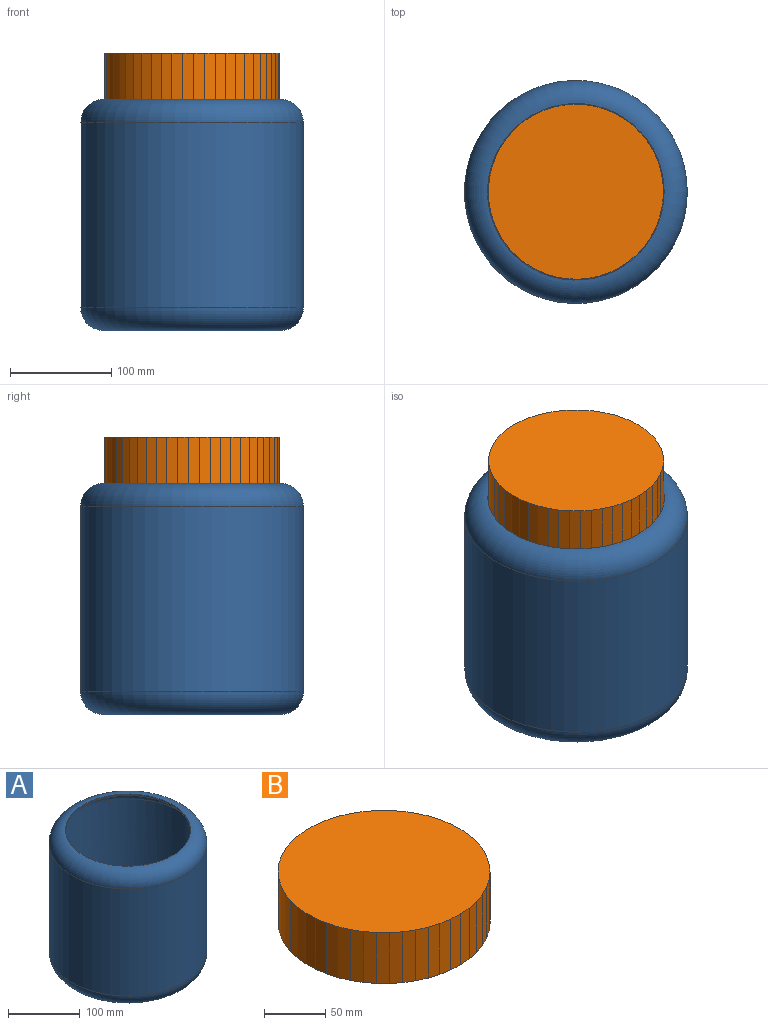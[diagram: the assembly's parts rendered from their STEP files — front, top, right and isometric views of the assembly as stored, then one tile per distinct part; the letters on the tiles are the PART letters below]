
ASSEMBLY  parts=2 mates=1
PART A: 9 faces, bbox 238.4x238.4x228.6 mm
  f0: cylinder r=110.11mm len=220.23mm, axis (0,0,-1), area 126529.7mm2, adj f2,f3
  f1: plane 174.51x174.51mm, normal (0,0,-1), area 23918.3mm2, adj f3
  f2: torus R=87.25mm, axis (0,0,1), area 22969.9mm2, adj f0,f4
  f3: torus R=87.25mm, axis (0,0,1), area 22969.9mm2, adj f0,f1
  f4: cylinder r=87.25mm len=174.51mm, axis (0,0,1), area 1392.5mm2, adj f2,f7
  f5: cylinder r=107.57mm len=215.15mm, axis (0,0,-1), area 123611.1mm2, adj f7,f8
  f6: plane 174.51x174.51mm, normal (0,0,1), area 23918.3mm2, adj f8
  f7: torus R=87.25mm, axis (0,0,1), area 20093.4mm2, adj f4,f5
  f8: torus R=87.25mm, axis (0,0,1), area 20093.4mm2, adj f5,f6
PART B: 52 faces, bbox 172.9x173x50.8 mm
  f0: plane 50.8x9.63mm, normal (0.89,-0.46,0), area 551.9mm2, adj f1,f49,f50,f51
  f1: plane 50.8x10.18mm, normal (0.94,-0.35,0), area 551.9mm2, adj f0,f2,f50,f51
  f2: plane 50.8x10.58mm, normal (0.97,-0.23,0), area 551.9mm2, adj f1,f3,f50,f51
  f3: plane 50.8x10.81mm, normal (0.99,-0.1,0), area 551.9mm2, adj f2,f4,f50,f51
  f4: plane 50.8x10.86mm, normal (1,0.02,0), area 551.9mm2, adj f3,f5,f50,f51
  f5: plane 50.8x10.75mm, normal (0.99,0.15,0), area 551.9mm2, adj f4,f6,f50,f51
  f6: plane 50.8x10.46mm, normal (0.96,0.27,0), area 551.9mm2, adj f5,f7,f50,f51
  f7: plane 50.8x10.02mm, normal (0.92,0.39,0), area 551.9mm2, adj f6,f8,f50,f51
  f8: plane 50.8x9.41mm, normal (0.87,0.5,0), area 551.9mm2, adj f7,f9,f50,f51
  f9: plane 50.8x8.65mm, normal (0.8,0.6,0), area 551.9mm2, adj f8,f10,f50,f51
  f10: plane 50.8x7.76mm, normal (0.71,0.7,0), area 551.9mm2, adj f9,f11,f50,f51
  f11: plane 50.8x8.52mm, normal (0.62,0.78,0), area 551.9mm2, adj f10,f12,f50,f51
  f12: plane 50.8x9.3mm, normal (0.52,0.86,0), area 551.9mm2, adj f11,f13,f50,f51
  f13: plane 50.8x9.93mm, normal (0.41,0.91,0), area 551.9mm2, adj f12,f14,f50,f51
  f14: plane 50.8x10.4mm, normal (0.29,0.96,0), area 551.9mm2, adj f13,f15,f50,f51
  f15: plane 50.8x10.71mm, normal (0.17,0.99,0), area 551.9mm2, adj f14,f16,f50,f51
  f16: plane 50.8x10.86mm, normal (0.04,1,0), area 551.9mm2, adj f15,f17,f50,f51
  f17: plane 50.8x10.83mm, normal (-0.08,1,0), area 551.9mm2, adj f16,f18,f50,f51
  f18: plane 50.8x10.63mm, normal (-0.21,0.98,0), area 551.9mm2, adj f17,f19,f50,f51
  f19: plane 50.8x10.26mm, normal (-0.33,0.94,0), area 551.9mm2, adj f18,f20,f50,f51
  f20: plane 50.8x9.73mm, normal (-0.44,0.9,0), area 551.9mm2, adj f19,f21,f50,f51
  f21: plane 50.8x9.05mm, normal (-0.55,0.83,0), area 551.9mm2, adj f20,f22,f50,f51
  f22: plane 50.8x8.22mm, normal (-0.65,0.76,0), area 551.9mm2, adj f21,f23,f50,f51
  f23: plane 50.8x8.08mm, normal (-0.74,0.67,0), area 551.9mm2, adj f22,f24,f50,f51
  f24: plane 50.8x8.92mm, normal (-0.82,0.57,0), area 551.9mm2, adj f23,f25,f50,f51
  f25: plane 50.8x9.63mm, normal (-0.89,0.46,0), area 551.9mm2, adj f24,f26,f50,f51
  f26: plane 50.8x10.18mm, normal (-0.94,0.35,0), area 551.9mm2, adj f25,f27,f50,f51
  f27: plane 50.8x10.58mm, normal (-0.97,0.23,0), area 551.9mm2, adj f26,f28,f50,f51
  f28: plane 50.8x10.81mm, normal (-0.99,0.1,0), area 551.9mm2, adj f27,f29,f50,f51
  f29: plane 50.8x10.86mm, normal (-1,-0.02,0), area 551.9mm2, adj f28,f30,f50,f51
  f30: plane 50.8x10.75mm, normal (-0.99,-0.15,0), area 551.9mm2, adj f29,f31,f50,f51
  f31: plane 50.8x10.46mm, normal (-0.96,-0.27,0), area 551.9mm2, adj f30,f32,f50,f51
  f32: plane 50.8x10.02mm, normal (-0.92,-0.39,0), area 551.9mm2, adj f31,f33,f50,f51
  f33: plane 50.8x9.41mm, normal (-0.87,-0.5,0), area 551.9mm2, adj f32,f34,f50,f51
  f34: plane 50.8x8.65mm, normal (-0.8,-0.6,0), area 551.9mm2, adj f33,f35,f50,f51
  f35: plane 50.8x7.76mm, normal (-0.71,-0.7,0), area 551.9mm2, adj f34,f36,f50,f51
  f36: plane 50.8x8.52mm, normal (-0.62,-0.78,0), area 551.9mm2, adj f35,f37,f50,f51
  f37: plane 50.8x9.3mm, normal (-0.52,-0.86,0), area 551.9mm2, adj f36,f38,f50,f51
  f38: plane 50.8x9.93mm, normal (-0.41,-0.91,0), area 551.9mm2, adj f37,f39,f50,f51
  f39: plane 50.8x10.4mm, normal (-0.29,-0.96,0), area 551.9mm2, adj f38,f40,f50,f51
  f40: plane 50.8x10.71mm, normal (-0.17,-0.99,0), area 551.9mm2, adj f39,f41,f50,f51
  f41: plane 50.8x10.86mm, normal (-0.04,-1,0), area 551.9mm2, adj f40,f42,f50,f51
  f42: plane 50.8x10.83mm, normal (0.08,-1,0), area 551.9mm2, adj f41,f43,f50,f51
  f43: plane 50.8x10.63mm, normal (0.21,-0.98,0), area 551.9mm2, adj f42,f44,f50,f51
  f44: plane 50.8x10.26mm, normal (0.33,-0.94,0), area 551.9mm2, adj f43,f45,f50,f51
  f45: plane 50.8x9.73mm, normal (0.44,-0.9,0), area 551.9mm2, adj f44,f46,f50,f51
  f46: plane 50.8x9.05mm, normal (0.55,-0.83,0), area 551.9mm2, adj f45,f47,f50,f51
  f47: plane 50.8x8.22mm, normal (0.65,-0.76,0), area 551.9mm2, adj f46,f48,f50,f51
  f48: plane 50.8x8.08mm, normal (0.74,-0.67,0), area 551.9mm2, adj f47,f49,f50,f51
  f49: plane 50.8x8.92mm, normal (0.82,-0.57,0), area 551.9mm2, adj f0,f48,f50,f51
  f50: plane 173x172.89mm, normal (0,0,1), area 23454.5mm2, adj f0,f1,f2,f3,f4,f5,f6,f7
  f51: plane 173x172.89mm, normal (0,0,-1), area 23454.5mm2, adj f0,f1,f2,f3,f4,f5,f6,f7
PLACE A t=(-112.04,2.69,-134.58)mm
PLACE B t=(-112.04,2.69,-0.27)mm
MATE slider A.f0 <-> B.f50  axis (0,0,-1) through (-112.04,2.69,-43.14)mm
